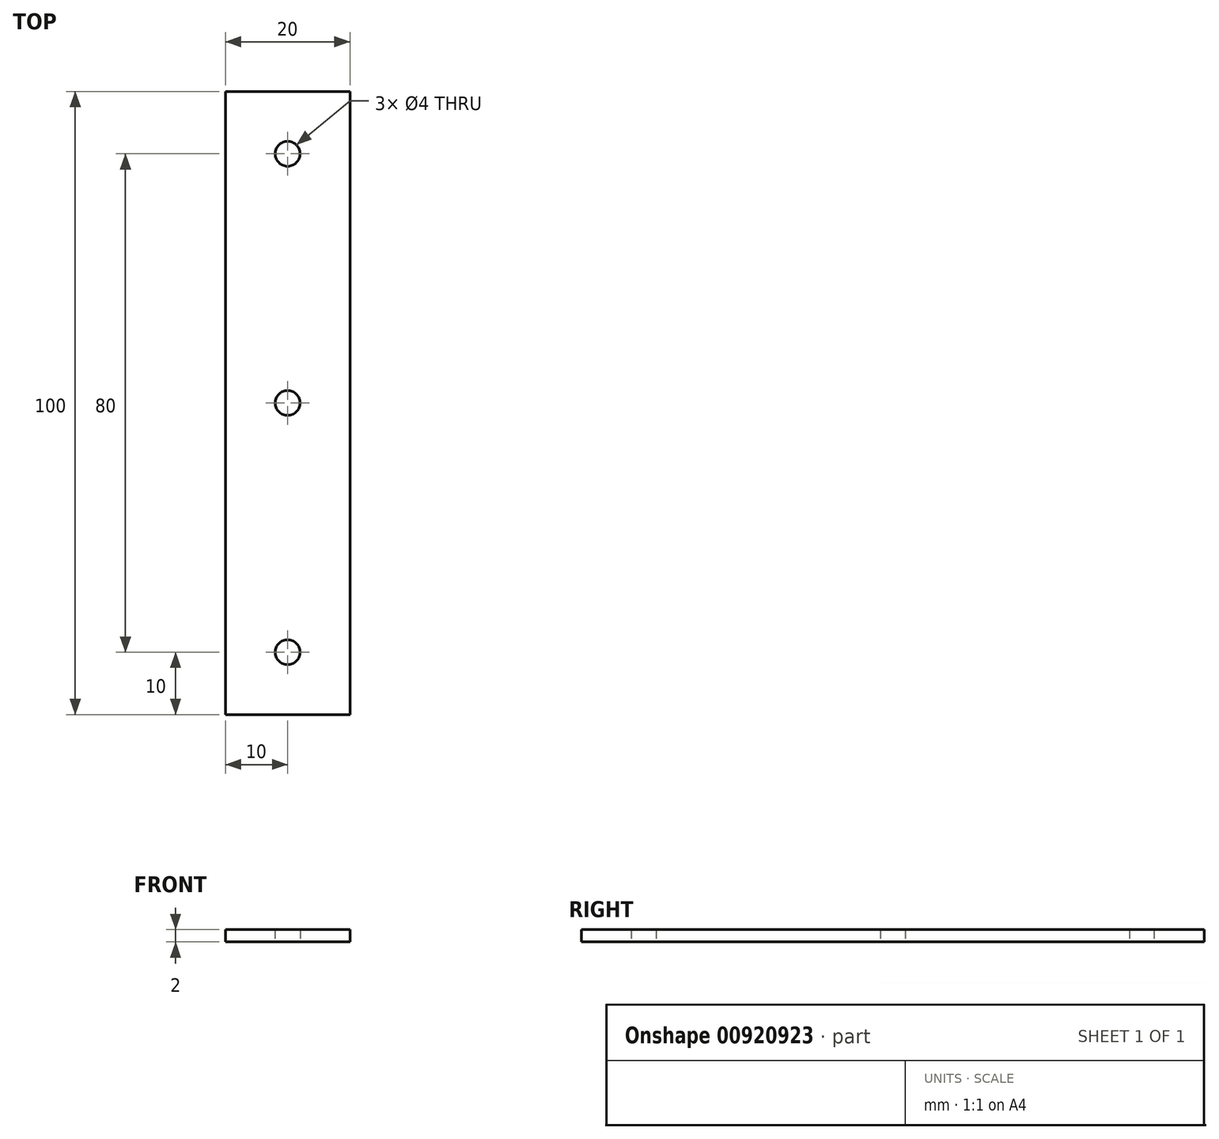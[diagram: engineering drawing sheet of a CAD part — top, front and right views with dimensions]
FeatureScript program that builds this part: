
annotation { "Feature Type Name" : "Feature", "Feature Type Description" : "" }
export const myFeature = defineFeature(function(context is Context, id is Id, definition is map)
    precondition{}
    {
        {
            var Q0;
            Q0=qCreatedBy(makeId("Top.planeOp"),FACE);
            var sketch = newSketch(context, id + "F0", { "sketchPlane" : qUnion([Q0])});
            skLineSegment(sketch, "E0.bottom", {"start": v(-10, 50) * mm, "end": v(10, 50) * mm});
            skLineSegment(sketch, "E0.top", {"start": v(-10, -50) * mm, "end": v(10, -50) * mm});
            skLineSegment(sketch, "E0.left", {"start": v(-10, 50) * mm, "end": v(-10, -50) * mm});
            skLineSegment(sketch, "E0.right", {"start": v(10, 50) * mm, "end": v(10, -50) * mm});
            skPoint(sketch, "E0.middle", {"position": v(0, 0) * mm});
            skCircle(sketch, "E1", {"center": v(0, 0) * mm, "radius": 2 * mm});
            skCircle(sketch, "E2", {"center": v(0, 40) * mm, "radius": 2 * mm});
            skCircle(sketch, "E3", {"center": v(0, -40) * mm, "radius": 2 * mm});
            skSolve(sketch);
        }
        {
            var Q0;
            Q0 = qSketchRegion(id + "F0", true);
            extrude(context, id + "F1", {"entities" : qUnion([Q0]), "depth" : 2 * mm, "offsetDistance" : 25 * mm});
        }
    });
